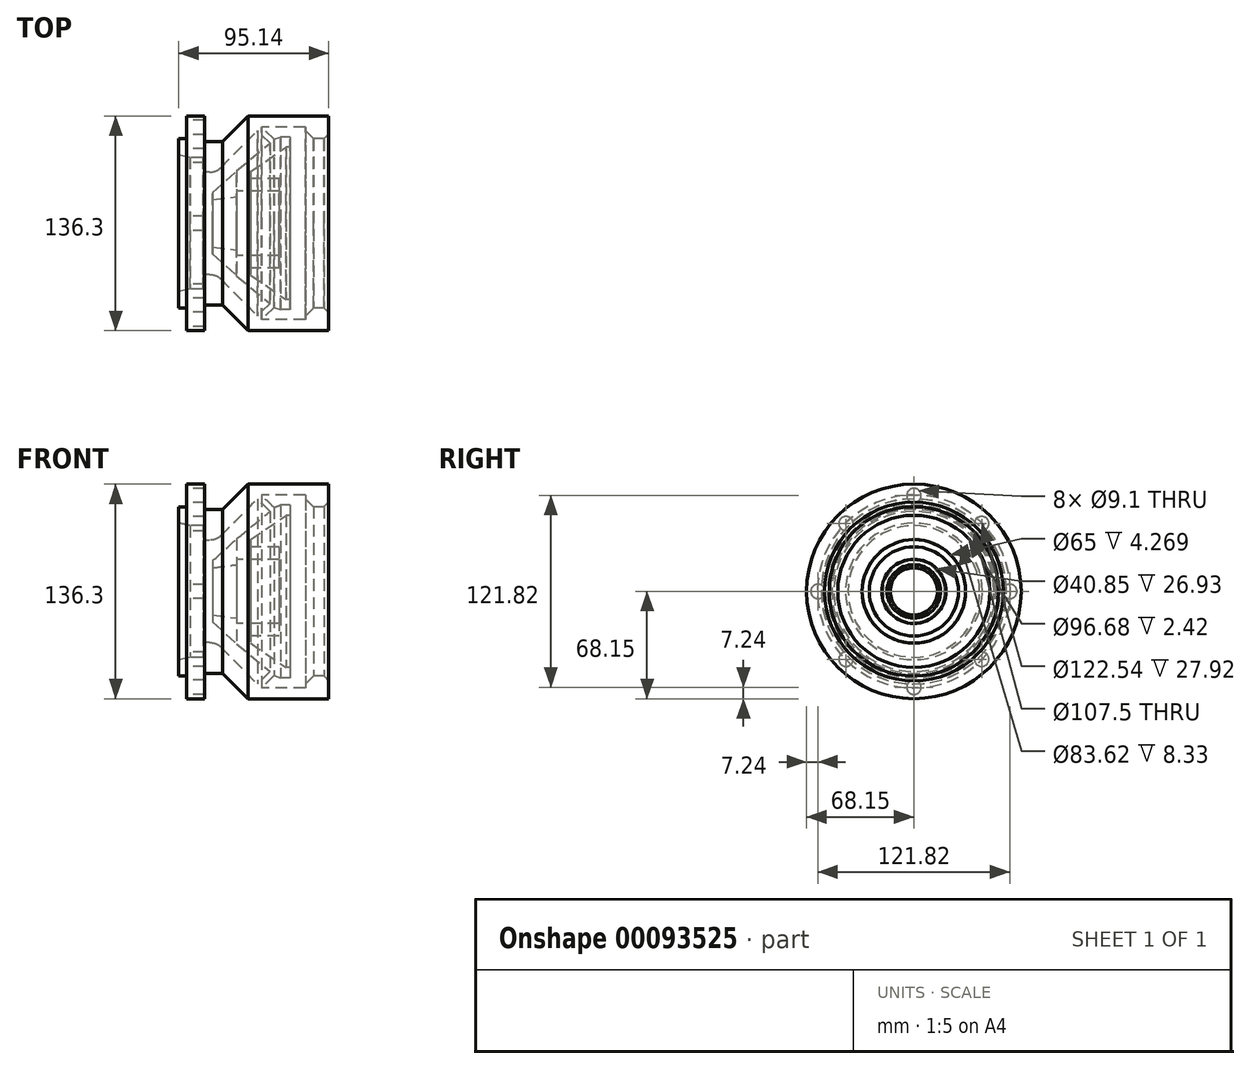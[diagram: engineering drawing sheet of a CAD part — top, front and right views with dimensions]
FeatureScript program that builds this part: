
annotation { "Feature Type Name" : "Feature", "Feature Type Description" : "" }
export const myFeature = defineFeature(function(context is Context, id is Id, definition is map)
    precondition{}
    {
        {
            var Q0;
            Q0=qCreatedBy(makeId("Front.planeOp"),FACE);
            var sketch = newSketch(context, id + "F0", { "sketchPlane" : qUnion([Q0])});
            skLineSegment(sketch, "E0", {"start": v(-50.65, 0) * mm, "end": v(44.5, 0) * mm, "construction": true});
            skLineSegment(sketch, "E1", {"start": v(-50.65, 0) * mm, "end": v(-50.65, 53.75) * mm});
            skLineSegment(sketch, "E2", {"start": v(-50.65, 53.75) * mm, "end": v(-45.65, 53.75) * mm});
            skLineSegment(sketch, "E3", {"start": v(-45.65, 53.75) * mm, "end": v(-45.65, 68.15) * mm});
            skLineSegment(sketch, "E4", {"start": v(-45.65, 68.15) * mm, "end": v(-34.1, 68.15) * mm});
            skLineSegment(sketch, "E5", {"start": v(44.5, 0) * mm, "end": v(44.5, 68.15) * mm});
            skLineSegment(sketch, "E6", {"start": v(44.5, 68.15) * mm, "end": v(-6.66, 68.15) * mm});
            skLineSegment(sketch, "E7", {"start": v(-51.12, 53.75) * mm, "end": v(-51.12, 43.45) * mm, "construction": true});
            skLineSegment(sketch, "E8", {"start": v(-50.65, 43.45) * mm, "end": v(-43.52, 43.45) * mm, "construction": true});
            skLineSegment(sketch, "E9", {"start": v(-43.52, 0) * mm, "end": v(-43.52, 41.81) * mm, "construction": true});
            skLineSegment(sketch, "E10", {"start": v(-50.65, 43.45) * mm, "end": v(-43.52, 41.81) * mm});
            skLineSegment(sketch, "E11", {"start": v(-43.52, 41.81) * mm, "end": v(-35.19, 41.81) * mm});
            skLineSegment(sketch, "E12", {"start": v(-35.19, 41.81) * mm, "end": v(-35.19, 32.5) * mm});
            skLineSegment(sketch, "E13", {"start": v(-35.19, 32.5) * mm, "end": v(-26.76, 32.5) * mm});
            skLineSegment(sketch, "E14", {"start": v(46.09, 68.15) * mm, "end": v(46.09, 53.75) * mm, "construction": true});
            skLineSegment(sketch, "E15", {"start": v(44.5, 53.75) * mm, "end": v(29.75, 53.75) * mm});
            skLineSegment(sketch, "E16", {"start": v(29.75, 53.75) * mm, "end": v(29.75, 61.27) * mm});
            skLineSegment(sketch, "E17", {"start": v(29.75, 61.27) * mm, "end": v(1.83, 61.27) * mm});
            skLineSegment(sketch, "E18", {"start": v(-34.1, 68.15) * mm, "end": v(-34.1, 52.05) * mm});
            skLineSegment(sketch, "E19", {"start": v(-34.1, 52.05) * mm, "end": v(-22.8, 52.05) * mm});
            skLineSegment(sketch, "E20", {"start": v(-22.8, 52.05) * mm, "end": v(-6.66, 68.15) * mm});
            skLineSegment(sketch, "E21", {"start": v(-26.76, 32.5) * mm, "end": v(1.83, 61.27) * mm, "construction": true});
            skLineSegment(sketch, "E22", {"start": v(-26.76, 32.5) * mm, "end": v(-5.61, 53.78) * mm});
            skLineSegment(sketch, "E23", {"start": v(1.83, 61.27) * mm, "end": v(9.8, 53.35) * mm});
            skLineSegment(sketch, "E24", {"start": v(1.83, 61.27) * mm, "end": v(-0.67, 58.75) * mm, "construction": true});
            skLineSegment(sketch, "E25", {"start": v(-0.67, 58.75) * mm, "end": v(7.3, 50.83) * mm});
            skLineSegment(sketch, "E26", {"start": v(9.8, 53.35) * mm, "end": v(20, 53.35) * mm, "construction": true});
            skLineSegment(sketch, "E27", {"start": v(20, 61.27) * mm, "end": v(20, 54.86) * mm, "construction": true});
            skLineSegment(sketch, "E28", {"start": v(20, 54.86) * mm, "end": v(14, 54.86) * mm});
            skLineSegment(sketch, "E29", {"start": v(9.8, 53.35) * mm, "end": v(14, 54.86) * mm});
            skLineSegment(sketch, "E30", {"start": v(-35.19, 32.5) * mm, "end": v(-35.19, 0) * mm, "construction": true});
            skLineSegment(sketch, "E31", {"start": v(-35.19, 3.49) * mm, "end": v(-29.09, 3.49) * mm, "construction": true});
            skLineSegment(sketch, "E32", {"start": v(-29.09, 0) * mm, "end": v(-29.09, 15) * mm});
            skLineSegment(sketch, "E33", {"start": v(-29.09, 15) * mm, "end": v(-29.09, 19.55) * mm, "construction": true});
            skLineSegment(sketch, "E34", {"start": v(-29.09, 15) * mm, "end": v(-13.79, 15) * mm, "construction": true});
            skLineSegment(sketch, "E35", {"start": v(-29.09, 15) * mm, "end": v(-13.79, 17.01) * mm});
            skLineSegment(sketch, "E36", {"start": v(-13.79, 17.01) * mm, "end": v(-13.79, 33.35) * mm, "construction": true});
            skLineSegment(sketch, "E37", {"start": v(-29.09, 19.55) * mm, "end": v(-13.79, 33.35) * mm});
            skLineSegment(sketch, "E38", {"start": v(-13.79, 33.35) * mm, "end": v(7.3, 50.83) * mm});
            skLineSegment(sketch, "E39", {"start": v(-13.79, 17.01) * mm, "end": v(-13.79, 20.42) * mm});
            skLineSegment(sketch, "E40", {"start": v(-13.79, 20.42) * mm, "end": v(13.14, 20.42) * mm});
            skLineSegment(sketch, "E41", {"start": v(-31.83, -15.12) * mm, "end": v(12.9, -15.12) * mm});
            skLineSegment(sketch, "E42", {"start": v(20, 54.86) * mm, "end": v(20, 48.34) * mm});
            skLineSegment(sketch, "E43", {"start": v(13.14, 20.42) * mm, "end": v(13.14, 28.33) * mm});
            skLineSegment(sketch, "E44", {"start": v(13.14, 28.33) * mm, "end": v(-5.16, 28.33) * mm});
            skLineSegment(sketch, "E45", {"start": v(-5.16, 28.33) * mm, "end": v(-5.16, 32.84) * mm});
            skLineSegment(sketch, "E46", {"start": v(20, 48.34) * mm, "end": v(17.58, 48.34) * mm});
            skLineSegment(sketch, "E47", {"start": v(-5.16, 32.84) * mm, "end": v(17.58, 48.34) * mm});
            skLineSegment(sketch, "E48", {"start": v(-5.61, 53.78) * mm, "end": v(-0.67, 58.75) * mm});
            skLineSegment(sketch, "E49", {"start": v(-29.09, 15) * mm, "end": v(-29.09, 19.55) * mm});
            skLineSegment(sketch, "E50", {"start": v(-26.76, 32.5) * mm, "end": v(-22.25, 28.02) * mm});
            skLineSegment(sketch, "E51", {"start": v(-22.25, 28.02) * mm, "end": v(-19.89, 30.15) * mm});
            skLineSegment(sketch, "E52", {"start": v(-19.89, 30.15) * mm, "end": v(-18.74, 28.88) * mm});
            skSolve(sketch);
        }
        {
            var Q0;
            {var subQ5=sQuery(id+"F0.wireOp",EDGE,"E2");Q0=makeQuery(id+"F0.imprint","IMPRINT",FACE,{"disambiguationData":[TD([[makeQuery(id+"F0.imprint","IMPRINT",EDGE,{"derivedFrom":subQ5}),-1.0]])]});}
            var Q1;
            Q1=sQuery(id+"F0.wireOp",EDGE,"E0");
            revolve(context, id + "F1", {"entities" : qUnion([Q0]), "axis" : qUnion([Q1]), "revolveType" : RevolveType.FULL});
        }
        {
            var Q0;
            Q0=makeQuery(id+"F1.opRevolve","SWEPT_FACE",FACE,{"disambiguationData":[OSD([sQuery(id+"F0.wireOp",EDGE,"E3")])]});
            var sketch = newSketch(context, id + "F2", { "sketchPlane" : qUnion([Q0])});
            skLineSegment(sketch, "E53", {"start": v(0, 53.75) * mm, "end": v(0, 56.36) * mm, "construction": true});
            skLineSegment(sketch, "E54", {"start": v(0, 56.36) * mm, "end": v(0, 60.9) * mm, "construction": true});
            skCircle(sketch, "E55", {"center": v(0, 60.9) * mm, "radius": 4.55 * mm});
            skCircle(sketch, "E56.1.0", {"center": v(-43.07, 43.07) * mm, "radius": 4.55 * mm});
            skCircle(sketch, "E56.2.0", {"center": v(-60.9, 0) * mm, "radius": 4.55 * mm});
            skCircle(sketch, "E56.3.0", {"center": v(-43.07, -43.07) * mm, "radius": 4.55 * mm});
            skCircle(sketch, "E56.4.0", {"center": v(0, -60.9) * mm, "radius": 4.55 * mm});
            skCircle(sketch, "E56.5.0", {"center": v(43.07, -43.07) * mm, "radius": 4.55 * mm});
            skCircle(sketch, "E56.6.0", {"center": v(60.9, 0) * mm, "radius": 4.55 * mm});
            skCircle(sketch, "E56.7.0", {"center": v(43.07, 43.07) * mm, "radius": 4.55 * mm});
            skPoint(sketch, "E56.center", {"position": v(0, 0) * mm});
            skSolve(sketch);
        }
        {
            var Q0;
            Q0=makeQuery(id+"F2.imprint","IMPRINT",FACE,{"disambiguationData":[TD([[makeQuery(id+"F2.imprint","IMPRINT",EDGE,{"derivedFrom":sQuery(id+"F2.wireOp",EDGE,"E55")}),1.0]])]});
            extrude(context, id + "F3", {"entities" : qUnion([Q0]), "operationType" : NewBodyOperationType.REMOVE, "oppositeDirection" : true, "depth" : 25.4 * mm});
        }
        {
            var Q0;
            Q0 = qSketchRegion(id + "F2", true);
            extrude(context, id + "F4", {"entities" : qUnion([Q0]), "operationType" : NewBodyOperationType.REMOVE, "oppositeDirection" : true, "depth" : 25.4 * mm});
        }
        {
            var Q0;
            Q0=makeQuery(id+"F1.opRevolve","SWEPT_EDGE",EDGE,{"disambiguationData":[OSD([sQuery(id+"F0.wireOp",EDGE,"E5"),sQuery(id+"F0.wireOp",EDGE,"E15")])]});
            chamfer(context, id + "F5", {"entities" : qUnion([Q0]), "width" : 3 * mm, "tangentPropagation" : true});
        }
        {
            var Q0;
            Q0=makeQuery(id+"F1.opRevolve","SWEPT_EDGE",EDGE,{"disambiguationData":[OSD([sQuery(id+"F0.wireOp",EDGE,"E13"),sQuery(id+"F0.wireOp",EDGE,"E22"),sQuery(id+"F0.wireOp",EDGE,"E50")])]});
            fillet(context, id + "F6", {"entities" : qUnion([Q0]), "radius" : 10 * mm, "tangentPropagation" : true, "allowEdgeOverflow" : false});
        }
        {
            var Q0;
            Q0=makeQuery(id+"F1.opRevolve","SWEPT_EDGE",EDGE,{"disambiguationData":[OSD([sQuery(id+"F0.wireOp",EDGE,"E15"),sQuery(id+"F0.wireOp",EDGE,"E16")])]});
            chamfer(context, id + "F7", {"entities" : qUnion([Q0]), "width" : 5.08 * mm, "tangentPropagation" : true});
        }
    });
